# Revit family: PRD_FrankeWS_Rosette_AQRM940
name_source: partatom
category: Generic Models
revit_build: Autodesk Revit 2018 (Build: 20190510_1515(x64)
units: mm (PartAtom-declared; Revit-internal decimal feet)

## family parameters
Can host rebar = No
Cut with Voids When Loaded = No
Host = Face
Part Type = Normal
Room Calculation Point = No
Round Connector Dimension = Use Diameter
Shared = No

## types (1)
- AQRM940
    AssetType = Fixed
    BIMObjectName = PRD_AR_Rosette_AQRM940
    Default Elevation = 0 mm  [stored 0 ft]
    Description = Chromium-plated rosette for drinking bubbler.
    DurationUnit = year
    GrossWeight = 0.04 kg
    IfcExportAs = IfcBuildingElementProxy
    IfcExportType = NOTDEFINED
    Manufacturer = KWC Group AG
    ManufacturerName = KWC Group AG
    ManufacturerURL = www.kwc.com
    Model = AQRM940
    ModelNumber = 2000101429
    ModelReference = AQRM940
    Name = Rosette for drinking bubbler AQRM940
    NetWeight = 0.04 kg
    NominalHeight = 0 mm  [stored 0 ft]
    NominalLength = 0 mm  [stored 0 ft]
    NominalWidth = 0 mm  [stored 0 ft]
    ProductInformation = https://pim.kwc.com
    RosetteMaterial = PRD_AR_ChromatedBrass_HighPolished
    URL = www.kwc.com
    Version = 1
    WarrantyDurationUnit = year

note: [stored X ft] marks values corroborated as IEEE doubles in the binary element streams (Revit-internal decimal feet)

## geometry (parser evidence)
native form markers: Sweep x3
no freeform markers — native parametric forms only
